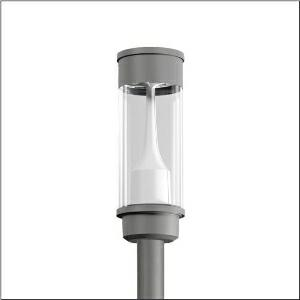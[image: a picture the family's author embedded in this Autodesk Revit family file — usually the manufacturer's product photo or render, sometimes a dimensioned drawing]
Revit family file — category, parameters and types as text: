
# Revit family: litepole_iq___pl1_2s_5xa5415jf14h_0c6a
name_source: partatom
category: Lighting Fixtures
units: mm (PartAtom-declared; Revit-internal decimal feet)

## family parameters
Cut with Voids When Loaded = No
Host = Face
Light Source = No
Part Type = Normal
Room Calculation Point = No
Round Connector Dimension = Use Diameter
Shared = No

## types (1)
- --- (1 x LED, 2970 lm, 19.3 W, 3000K)
    Apparent Load = 19 VA
    CIE Flux Codes = 23 62 94 96 100
    Color Rendering = 70
    Color Temperature = 3000K
    Default Elevation = 1800 mm
    Description = Litepole iQ, mast luminaire, Module 540 iQ-SR, primary light control with 3 zone facetted reflector, of plastic, silver coated, highly specular, structured, primary optical cover: cover, of PMMA, transparent, light distribution: PL1.2s, light emission: direct distribution, primary light characteristic: symmetric, installation type: post-top, LED, High Power LED, rated luminous flux: 2.970lm, luminous efficacy: 154lm/W, light colour: 730, colour temperature: 3000K, control gear: iQ Street-Remote, control: Auto-Match, Temp-Guard, Lumen-Switch, Night-Set, Smart-Wire, Light-Fading, Desk-Remote (wireless, voltage-free reading and setting of iQ features in the workshop via application-optimized NFC function/RFID function), optimised constant luminous flux control (CLO 2.0), Street-Remote, pre-setting: logarithmic dimming characteristic, with terminal, 6-pole, max. 2.5mm², mains connection: 230..240V, AC, 50/60Hz, start of lifetime: 19W, end of service life: 21W, reduction: 10W, luminaire housing, upper part, of glass-fibre reinforced polyester, coated, Siteco® metallic grey (DB 702S), diameter: 210mm, height: 590mm, spigot size: d x l = 76 x 70mm (post-top) | with reducer (optional accessory) 60 x 70mm, mounting height: 3..5m, post-top mast mounting element, of diecast aluminium, coated, Siteco® metallic grey (DB 702S), Module 540 iQ-SR, traffic white (RAL 9016), equipment: standard, protection rating (complete): IP65, insulation class (complete): insulation class II (safety insulation), certification: CE, ENEC, VDE, packaging unit: 1 piece

Light Distribution: PL1.2s
    Height = 590 mm
    Lamp = 1 x LED
    Lamp Light Flux = 2970 lm
    Lamp Power = 19.3 W
    Lamp count = 1
    Length = 220 mm
    Luminous efficacy = 154 lm/W
    Manufacturer = Siteco
    ModVariant = No
    Model = 5XA5415JF14H
    Number of Poles = 1
    OnlyDefault = Yes
    Power Factor = 1
    Product Name = Litepole iQ | PL1.2s
    Product group = mast luminaire | pylon top
    ProductGroupID = 6100
    Protection Class = Protection class II
    Protection Degree = IP 65
    RLX_Detail_Level = 1
    RLX_Emergency_Light_Flux = 0 lm
    RLX_Emergency_Type = 0
    RLX_Emergency_Type_DB = No
    RlxData = <blob elided: 39589 chars, md5=8f0aa569>
    Socket = socket
    Standby Power = 0 W
    System Light Flux = 2970 lm
    System Power = 19 W
    Type Comments = factory setting: luminous flux: 100 % | dim-lin: 254 | 403 mA
    Type Image = l_1006025.jpg
    URL = http://relux.com
    VarID = @adj_144323
    Voltage = 0 V
    Weight = 0.00 kg
    Width = 0 mm  [stored 0 ft]

note: [stored X ft] marks values corroborated as IEEE doubles in the binary element streams (Revit-internal decimal feet)

## geometry (parser evidence)
native form markers: Blend x4, Sweep x9
no freeform markers — native parametric forms only
